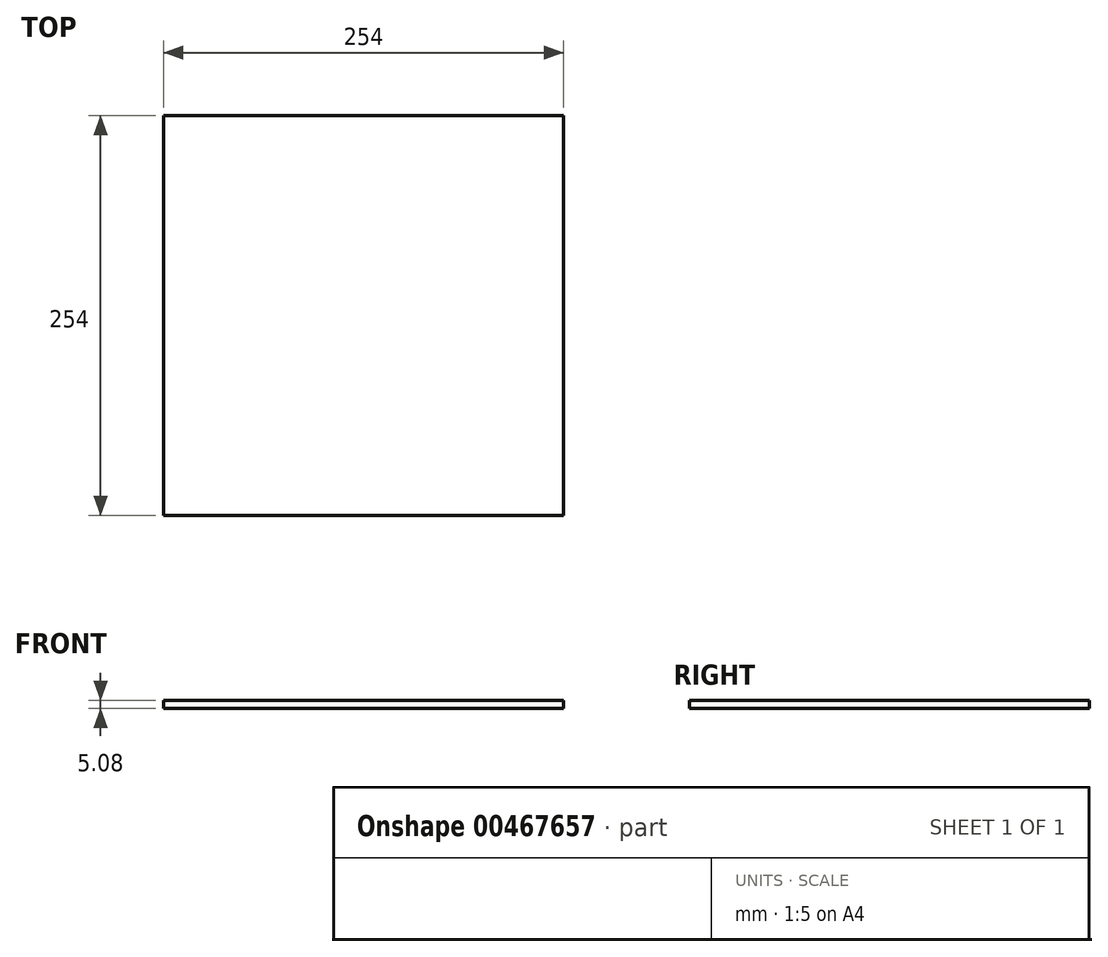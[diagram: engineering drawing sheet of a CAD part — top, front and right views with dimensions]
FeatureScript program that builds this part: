
annotation { "Feature Type Name" : "Feature", "Feature Type Description" : "" }
export const myFeature = defineFeature(function(context is Context, id is Id, definition is map)
    precondition{}
    {
        {
            var Q0;
            Q0=qCreatedBy(makeId("Top.planeOp"),FACE);
            var sketch = newSketch(context, id + "F0", { "sketchPlane" : qUnion([Q0])});
            skLineSegment(sketch, "E0.bottom", {"start": v(127, 127) * mm, "end": v(-127, 127) * mm});
            skLineSegment(sketch, "E0.top", {"start": v(127, -127) * mm, "end": v(-127, -127) * mm});
            skLineSegment(sketch, "E0.left", {"start": v(127, 127) * mm, "end": v(127, -127) * mm});
            skLineSegment(sketch, "E0.right", {"start": v(-127, 127) * mm, "end": v(-127, -127) * mm});
            skPoint(sketch, "E0.middle", {"position": v(0, 0) * mm});
            skSolve(sketch);
        }
        {
            var Q0;
            Q0=makeQuery(id+"F0.imprint","IMPRINT",FACE,{"disambiguationData":[TD([[makeQuery(id+"F0.imprint","IMPRINT",EDGE,{"derivedFrom":sQuery(id+"F0.wireOp",EDGE,"E0.bottom")}),1.0]])]});
            extrude(context, id + "F1", {"entities" : qUnion([Q0]), "depth" : 5.08 * mm});
        }
    });
